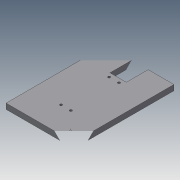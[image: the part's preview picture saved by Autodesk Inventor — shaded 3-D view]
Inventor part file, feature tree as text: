
AUTODESK INVENTOR PART (.ipt)
format: ipt  version: 2014 SP1 (Build 180222100, 222)  size: 146,944 bytes
history: native  units: in
note: dims shown in document units (in); Inventor stores cm internally (conversion verified against a paired STEP export)
features: extrude x3, sketch x2, fillet x1, pattern_linear x1
ambient origin geometry x8: Origin, YZ Plane, XZ Plane, XY Plane, X Axis, Y Axis, Z Axis, Center Point
bodies: Solid1 (feature_tree)
feature tree (7):
  extrude  "Extrusion1"  Depth=0.1969in
  extrude  "Extrusion4"  Depth=2.0079in
  extrude  "Extrusion5"  Depth=2.0079in
  fillet  "Fillet1"  Radius=0.1772in
  pattern_linear  "Rectangular Pattern4"  Spacing1=0.1772in  [1 undecoded]
  sketch  "Sketch4"  dims[d2=0.1969in d3=0.0in d4=0.0886in]
  sketch  "Sketch5"  dims[d5=0.0886in d6=0.8661in d7=0.8661in d8=0.1772in d9=0.1772in d28=0.4331in d29=0.315in d30=0.0in d31=0.7874in d32=0.4331in d33=0.0in d34=0.1181in d35=0.1181in d36=0.2165in d37=0.315in d38=0.0in d45=0.7874in d46=0.1181in d55=0.7874in d57=3.2874in d58=0.7874in d60=2.0079in]
note: 1 required parameter value undecoded (feature->parameter linkage not recoverable at this tier; creation-order binding heuristic only, values carry confidence <= 0.55)
